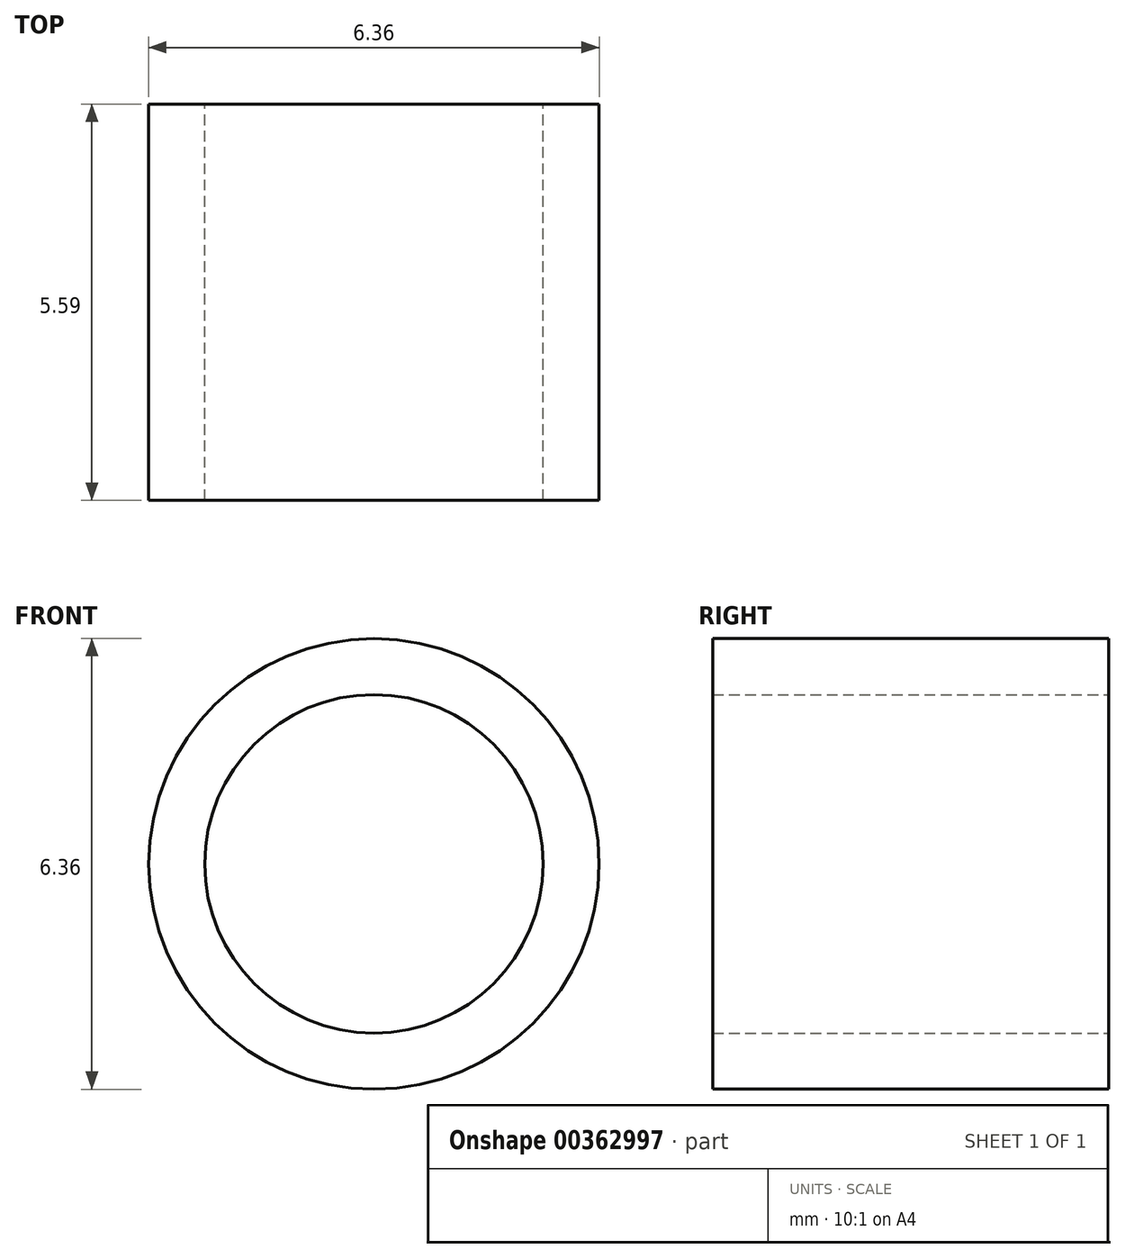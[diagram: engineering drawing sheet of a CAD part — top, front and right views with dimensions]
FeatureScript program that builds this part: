
annotation { "Feature Type Name" : "Feature", "Feature Type Description" : "" }
export const myFeature = defineFeature(function(context is Context, id is Id, definition is map)
    precondition{}
    {
        {
            var Q0;
            Q0=qCreatedBy(makeId("Front.planeOp"),FACE);
            var sketch = newSketch(context, id + "F0", { "sketchPlane" : qUnion([Q0])});
            skCircle(sketch, "E0", {"center": v(0, 0) * mm, "radius": 2.39 * mm});
            skCircle(sketch, "E1", {"center": v(0, 0) * mm, "radius": 3.18 * mm});
            skSolve(sketch);
        }
        {
            var Q0;
            Q0=makeQuery(id+"F0.imprint","IMPRINT",FACE,{"disambiguationData":[TD([[makeQuery(id+"F0.imprint","IMPRINT",EDGE,{"derivedFrom":sQuery(id+"F0.wireOp",EDGE,"E0")}),-1.0]])]});
            extrude(context, id + "F1", {"entities" : qUnion([Q0]), "depth" : 5.6 * mm});
        }
    });
